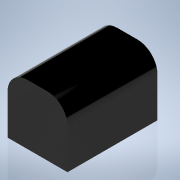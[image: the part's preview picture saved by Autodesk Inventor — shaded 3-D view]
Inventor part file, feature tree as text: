
AUTODESK INVENTOR PART (.ipt)
format: ipt  version: 2021 (Build 250183000, 183)  size: 211,456 bytes
history: native  units: mm
features: extrude x4, sketch x4, fillet x1
ambient origin geometry x8: Origin, YZ Plane, XZ Plane, XY Plane, X Axis, Y Axis, Z Axis, Center Point
bodies: Solid1 (feature_tree)
feature tree (9):
  extrude  "Extrusion1"  Depth=60.0mm
  fillet  "Fillet1"  Radius=60.0mm
  extrude  "Extrusion2"  Depth=20.0mm
  extrude  "Extrusion3"  Depth=15.0mm
  extrude  "Extrusion4"  Depth=30.0mm TaperAngle=0.0deg
  sketch  "Sketch1"  dims[d0=90.0mm d1=60.0mm d2=60.0mm d3=0.0mm]
  sketch  "Sketch2"  dims[d4=20.0mm d6=20.0mm]
  sketch  "Sketch3"  dims[d7=15.0mm d8=0.0mm d9=2.0mm]
  sketch  "Sketch4"  dims[d10=150.0mm d12=360.0deg d14=30.0mm d15=0.0mm d16=20.0mm d17=15.0mm d18=0.0mm d19=30.0mm d20=30.0mm]
